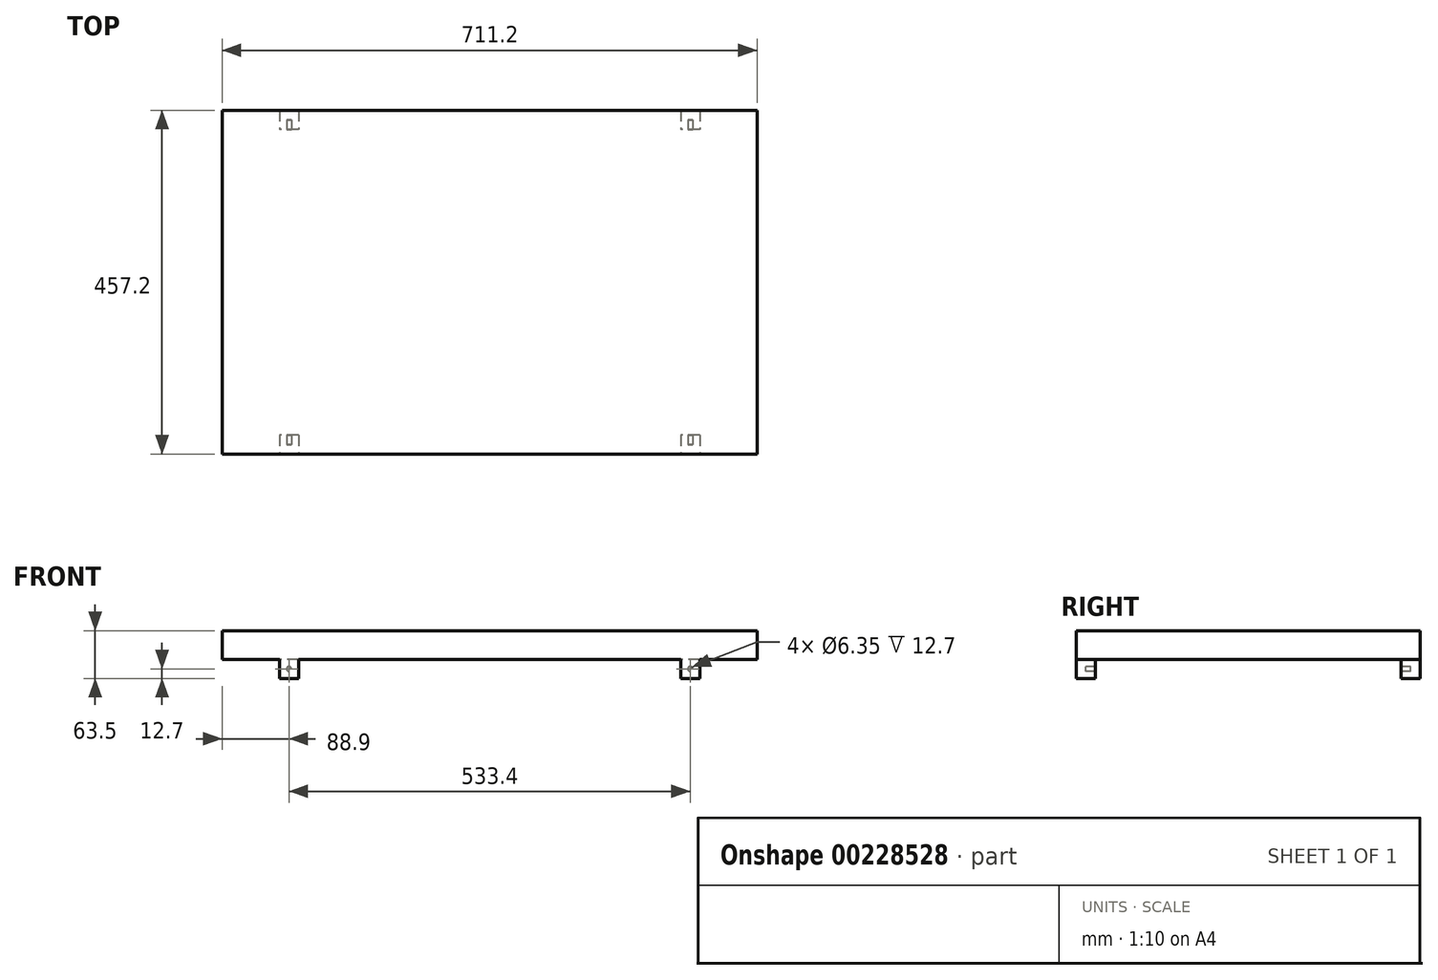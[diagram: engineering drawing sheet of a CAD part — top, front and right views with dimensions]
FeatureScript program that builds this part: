
annotation { "Feature Type Name" : "Feature", "Feature Type Description" : "" }
export const myFeature = defineFeature(function(context is Context, id is Id, definition is map)
    precondition{}
    {
        {
            var Q0;
            Q0=qCreatedBy(makeId("Front.planeOp"),FACE);
            var sketch = newSketch(context, id + "F0", { "sketchPlane" : qUnion([Q0])});
            skLineSegment(sketch, "E0", {"start": v(0, 63.5) * mm, "end": v(711.2, 63.5) * mm});
            skLineSegment(sketch, "E1", {"start": v(711.2, 63.5) * mm, "end": v(711.2, 25.4) * mm});
            skLineSegment(sketch, "E2", {"start": v(711.2, 25.4) * mm, "end": v(0, 25.4) * mm});
            skLineSegment(sketch, "E3", {"start": v(0, 25.4) * mm, "end": v(0, 63.5) * mm});
            skLineSegment(sketch, "E4", {"start": v(76.2, 25.4) * mm, "end": v(76.2, 0) * mm});
            skLineSegment(sketch, "E5", {"start": v(76.2, 0) * mm, "end": v(101.6, 0) * mm});
            skLineSegment(sketch, "E6", {"start": v(101.6, 0) * mm, "end": v(101.6, 25.4) * mm});
            skLineSegment(sketch, "E7", {"start": v(609.6, 25.4) * mm, "end": v(609.6, 0) * mm});
            skLineSegment(sketch, "E8", {"start": v(609.6, 0) * mm, "end": v(635, 0) * mm});
            skLineSegment(sketch, "E9", {"start": v(635, 0) * mm, "end": v(635, 25.4) * mm});
            skLineSegment(sketch, "E10", {"start": v(76.2, 25.4) * mm, "end": v(101.6, 0) * mm, "construction": true});
            skLineSegment(sketch, "E11", {"start": v(609.6, 25.4) * mm, "end": v(635, 0) * mm, "construction": true});
            skCircle(sketch, "E12", {"center": v(622.3, 12.7) * mm, "radius": 3.18 * mm});
            skCircle(sketch, "E13", {"center": v(88.9, 12.7) * mm, "radius": 3.18 * mm});
            skSolve(sketch);
        }
        {
            var Q0;
            Q0=makeQuery(id+"F0.imprint","IMPRINT",FACE,{"disambiguationData":[TD([[makeQuery(id+"F0.imprint","IMPRINT",EDGE,{"derivedFrom":sQuery(id+"F0.wireOp",EDGE,"E0")}),-1.0]])]});
            extrude(context, id + "F1", {"entities" : qUnion([Q0]), "oppositeDirection" : true, "depth" : 457.2 * mm});
        }
        {
            var Q0;
            {var subQ0=sQuery(id+"F0.wireOp",EDGE,"E4");Q0=makeQuery(id+"F0.imprint","IMPRINT",FACE,{"disambiguationData":[TD([[makeQuery(id+"F0.imprint","IMPRINT",EDGE,{"derivedFrom":subQ0}),1.0]])]});}
            var Q1;
            {var subQ0=sQuery(id+"F0.wireOp",EDGE,"E7");Q1=makeQuery(id+"F0.imprint","IMPRINT",FACE,{"disambiguationData":[TD([[makeQuery(id+"F0.imprint","IMPRINT",EDGE,{"derivedFrom":subQ0}),1.0]])]});}
            var Q2;
            Q2=makeQuery(id+"F0.imprint","IMPRINT",FACE,{"disambiguationData":[TD([[makeQuery(id+"F0.imprint","IMPRINT",EDGE,{"derivedFrom":sQuery(id+"F0.wireOp",EDGE,"E13")}),1.0]])]});
            var Q3;
            Q3=makeQuery(id+"F0.imprint","IMPRINT",FACE,{"disambiguationData":[TD([[makeQuery(id+"F0.imprint","IMPRINT",EDGE,{"derivedFrom":sQuery(id+"F0.wireOp",EDGE,"E12")}),1.0]])]});
            extrude(context, id + "F2", {"entities" : qUnion([Q0, Q1, Q2, Q3]), "operationType" : NewBodyOperationType.ADD, "oppositeDirection" : true, "depth" : 25.4 * mm});
        }
        {
            var Q0;
            {var subQ0=sQuery(id+"F0.wireOp",EDGE,"E4");Q0=makeQuery(id+"F0.imprint","IMPRINT",FACE,{"disambiguationData":[TD([[makeQuery(id+"F0.imprint","IMPRINT",EDGE,{"derivedFrom":subQ0}),1.0]])]});}
            var Q1;
            {var subQ0=sQuery(id+"F0.wireOp",EDGE,"E7");Q1=makeQuery(id+"F0.imprint","IMPRINT",FACE,{"disambiguationData":[TD([[makeQuery(id+"F0.imprint","IMPRINT",EDGE,{"derivedFrom":subQ0}),1.0]])]});}
            var Q2;
            Q2=makeQuery(id+"F0.imprint","IMPRINT",FACE,{"disambiguationData":[TD([[makeQuery(id+"F0.imprint","IMPRINT",EDGE,{"derivedFrom":sQuery(id+"F0.wireOp",EDGE,"E12")}),1.0]])]});
            var Q3;
            Q3=makeQuery(id+"F0.imprint","IMPRINT",FACE,{"disambiguationData":[TD([[makeQuery(id+"F0.imprint","IMPRINT",EDGE,{"derivedFrom":sQuery(id+"F0.wireOp",EDGE,"E13")}),1.0]])]});
            var Q4;
            Q4=makeQuery(id+"F1.opExtrude","CAP_FACE",FACE,{"disambiguationData":[OSD([sQuery(id+"F0.wireOp",EDGE,"E0"),sQuery(id+"F0.wireOp",EDGE,"E1"),sQuery(id+"F0.wireOp",EDGE,"E2"),sQuery(id+"F0.wireOp",EDGE,"E3")])],"isStart":false});
            extrude(context, id + "F3", {"entities" : qUnion([Q0, Q1, Q2, Q3]), "operationType" : NewBodyOperationType.ADD, "endBound" : BoundingType.UP_TO_SURFACE, "oppositeDirection" : true, "endBoundEntityFace" : qUnion([Q4]), "depth" : 25.4 * mm, "hasSecondDirection" : true, "secondDirectionOppositeDirection" : true, "secondDirectionDepth" : 431.8 * mm});
        }
        {
            var Q0;
            Q0=makeQuery(id+"F0.imprint","IMPRINT",FACE,{"disambiguationData":[TD([[makeQuery(id+"F0.imprint","IMPRINT",EDGE,{"derivedFrom":sQuery(id+"F0.wireOp",EDGE,"E13")}),1.0]])]});
            var Q1;
            Q1=makeQuery(id+"F0.imprint","IMPRINT",FACE,{"disambiguationData":[TD([[makeQuery(id+"F0.imprint","IMPRINT",EDGE,{"derivedFrom":sQuery(id+"F0.wireOp",EDGE,"E12")}),1.0]])]});
            extrude(context, id + "F4", {"entities" : qUnion([Q0, Q1]), "operationType" : NewBodyOperationType.REMOVE, "oppositeDirection" : true, "depth" : 444.5 * mm, "hasSecondDirection" : true, "secondDirectionOppositeDirection" : true, "secondDirectionDepth" : 12.7 * mm});
        }
    });
